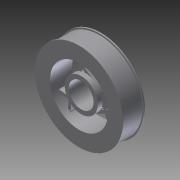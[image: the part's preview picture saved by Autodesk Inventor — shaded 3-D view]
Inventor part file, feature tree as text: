
AUTODESK INVENTOR PART (.ipt)
format: ipt  version: 2012 (Build 160160000, 160)  size: 243,200 bytes
history: native  units: in
note: dims shown in document units (in); Inventor stores cm internally (conversion verified against a paired STEP export)
features: extrude x5, sketch x1, fillet x1
ambient origin geometry x8: Origin, YZ Plane, XZ Plane, XY Plane, X Axis, Y Axis, Z Axis, Center Point
bodies: Solid1 (feature_tree)
feature tree (7):
  sketch  "Sketch1"  dims[d0=4.0in d1=1.5in d2=3.875in d3=2.625in d15=0.8in d16=0.0in d17=1.0in d18=0.0in d19=1.0in d20=0.0in d21=0.875in d22=0.0in d71=1.125in d81=0.3507in d82=0.4676in d83=0.3507in d84=0.4676in d85=1.1811in d87=360.0deg d91=0.0625in d92=0.0625in d93=0.375in d94=0.0in d96=0.0625in d97=0.0625in d98=0.0312in d99=0.0625in d100=0.0625in d101=0.0625in d103=0.0625in]
  extrude  "Extrusion1"  Depth=1.5in
  extrude  "Extrusion2"  Depth=3.875in
  extrude  "Extrusion3"  Depth=2.625in
  extrude  "Extrusion4"  Depth=0.8in TaperAngle=0.0deg
  extrude  "Extrusion6"  Depth=1.0in TaperAngle=0.0deg
  fillet  "Fillet3"  Radius=1.0in
